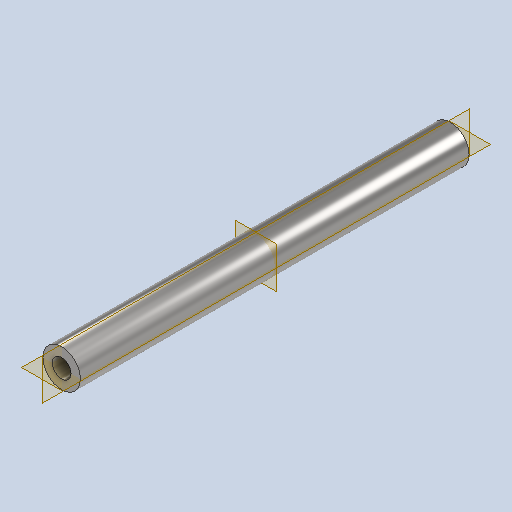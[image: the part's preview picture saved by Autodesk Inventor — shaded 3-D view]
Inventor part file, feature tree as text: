
AUTODESK INVENTOR PART (.ipt)
format: ipt  version: 2025.2 (Build 292293000, 293)  size: 126,464 bytes
history: native  units: mm
features: other x1, extrude x1, sketch x1
ambient origin geometry x8: Origin, YZ Plane, XZ Plane, XY Plane, X Axis, Y Axis, Z Axis, Center Point
bodies: Body1 (feature_tree)
feature tree (3):
  other  "Sólido1"
  extrude  "Extrusão1"  Depth=35.0mm
  sketch  "Esboço1"  dims[d0=70.0mm d1=35.0mm d2=725.0mm d3=0.0mm]
